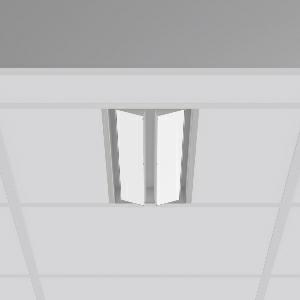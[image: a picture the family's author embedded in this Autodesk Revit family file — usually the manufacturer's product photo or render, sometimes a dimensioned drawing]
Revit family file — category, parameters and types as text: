
# Revit family: tx-move_901739_004_1_7426
name_source: partatom
category: Lighting Fixtures
units: mm (PartAtom-declared; Revit-internal decimal feet)

## family parameters
Cut with Voids When Loaded = No
Host = Face
Light Source = No
Part Type = Normal
Room Calculation Point = No
Round Connector Dimension = Use Diameter
Shared = No

## types (1)
- MultiLumen 1 (1 x LED Modul 840, 2450 lm, 4000)
    Apparent Load = 35 VA
    Approval mark = CE
    CIE Flux Codes = 47 79 96 100 100
    Color Rendering = 80
    Color Temperature = 4000
    Default Elevation = 1800 mm
    Description = Series: TX-MOVE
Einlege/Einbau-Flächenstrahler. Housing: sheet steel, powder-coated. 2xSwivel range: 90°. High-efficiency LED units with flush-mounted opal diffuser made of non-yellowing PMMA. Symmetrical wide beam light emission. Suitable for laying in grid ceiling module 625. Connected converter included in separate gearbox.Suitable for through-wiring.MultiLumen: Luminous flux adjustable in 3 steps. Accessories: Mounting frame for installation in suspended ceilings. Environmentally friendly and resource-saving due to replaceable and recyclable components. 
Colour: silver, matt (approx. RAL 9006)
Length: 622 mm
Width: 190 mm
Height: 39 mm
Cut-out length: 602 mm
Cut-out width: 174 mm
Recess height: 100 mm
Lamp: LED
Socket: without socket
Colour temperature: 4000K
Colour rendering index (CRI): 80
System power: 35 W
Rated luminous flux: 4900 lm
Luminous efficiency: 140 lm/W
System power 2: 47 W
Rated luminous flux 2: 6450 lm
Luminous efficiency 2: 137 lm/W
System power 3: 68 W
Rated luminous flux 3: 8750 lm
Luminous efficiency 3: 129 lm/W
Control gear: Regulated power supply
Protection class: I
Type of protection: IP 20
    Height = 0 mm  [stored 0 ft]
    Lamp = 1 x LED Modul 840
    Lamp Light Flux = 2450 lm
    Lamp count = 1
    Length = 622 mm
    Lifetime = 50000 h
    Luminous efficacy = 140 lm/W
    Manufacturer = RZB
    ModVariant = No
    Model = 901739.004.1
    Mounting Place = Ceiling, Wall
    Mounting Type = Recessed
    Number of Poles = 1
    OnlyDefault = Yes
    Power Factor = 1
    Product Name = TX-MOVE
    Product group = Recessed projectors
    ProductGroupID = 401
    Protection Class = Protection class I
    Protection Degree = IP 20
    RLX_Detail_Level = 1
    RLX_Emergency_Light_Flux = 0 lm
    RLX_Emergency_Type = 0
    RLX_Emergency_Type_DB = No
    RlxData = <blob elided: 29941 chars, md5=bb84d7b9>
    Socket = socket
    Standby Power = 0 W
    System Light Flux = 4900 lm
    System Power = 35 W
    Type Comments = MultiLumen 1
    Type Image = 901739.004.jpg
    URL = http://relux.com
    VarID = multilumen_1
    Voltage = 230 V
    Voltage Range = 220-240 V
    Weight = 0.00 kg
    Width = 190 mm  [stored 0.62336 ft]

note: [stored X ft] marks values corroborated as IEEE doubles in the binary element streams (Revit-internal decimal feet)

## geometry (parser evidence)
native form markers: Blend x4, Sweep x17
no freeform markers — native parametric forms only
